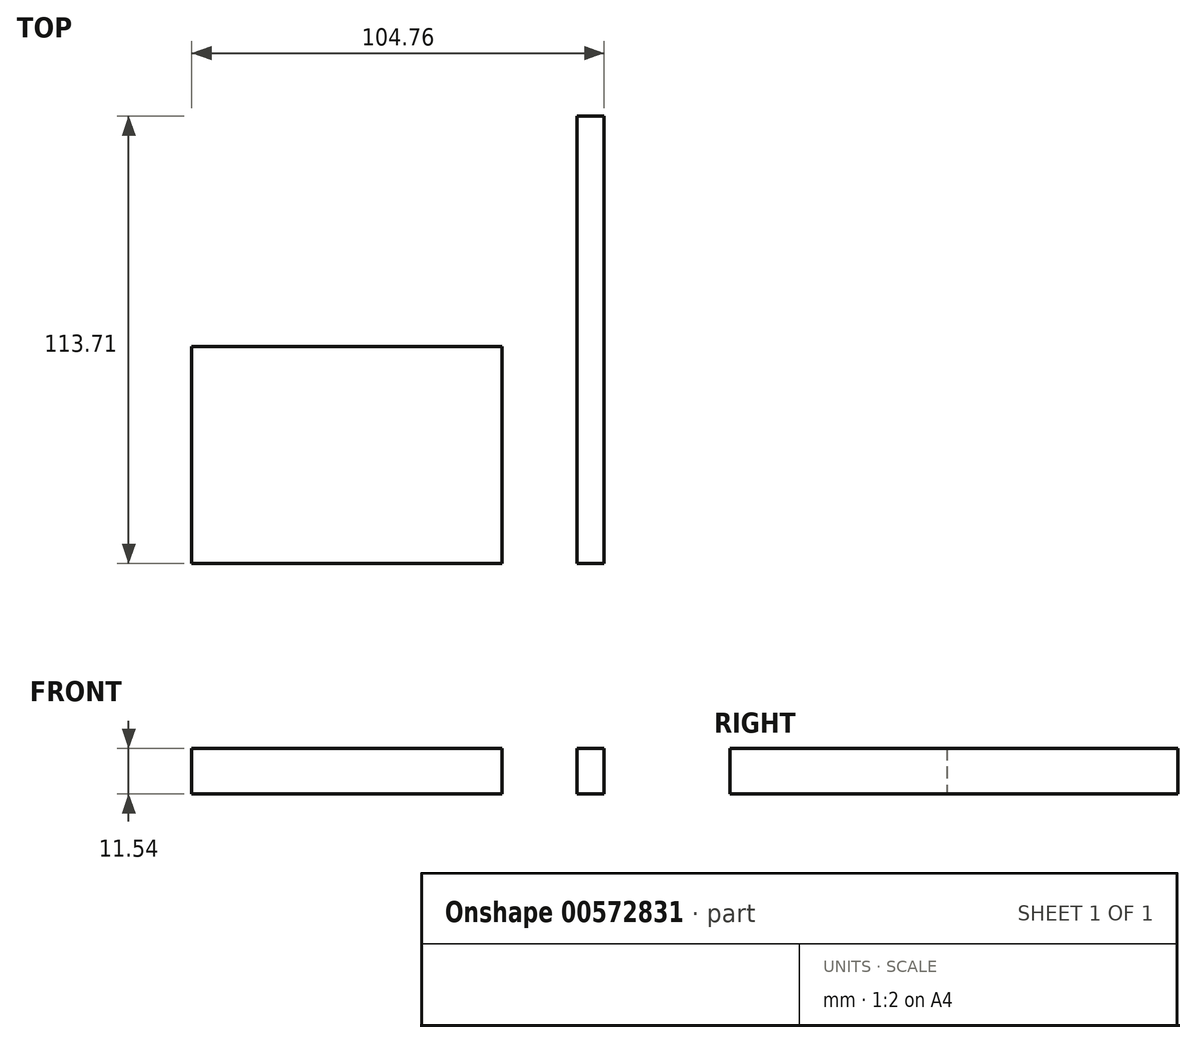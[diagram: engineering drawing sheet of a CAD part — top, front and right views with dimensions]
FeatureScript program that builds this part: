
annotation { "Feature Type Name" : "Feature", "Feature Type Description" : "" }
export const myFeature = defineFeature(function(context is Context, id is Id, definition is map)
    precondition{}
    {
        {
            var Q0;
            Q0=qCreatedBy(makeId("Top.planeOp"),FACE);
            var sketch = newSketch(context, id + "F0", { "sketchPlane" : qUnion([Q0])});
            skLineSegment(sketch, "E0.bottom", {"start": v(49.78, -55.1) * mm, "end": v(56.7, -55.1) * mm});
            skLineSegment(sketch, "E0.top", {"start": v(49.78, 58.61) * mm, "end": v(56.7, 58.61) * mm});
            skLineSegment(sketch, "E0.left", {"start": v(49.78, -55.1) * mm, "end": v(49.78, 58.61) * mm});
            skLineSegment(sketch, "E0.right", {"start": v(56.7, -55.1) * mm, "end": v(56.7, 58.61) * mm});
            skLineSegment(sketch, "E1.bottom", {"start": v(-48.05, 0) * mm, "end": v(30.72, 0) * mm});
            skLineSegment(sketch, "E1.top", {"start": v(-48.05, -55.1) * mm, "end": v(30.72, -55.1) * mm});
            skLineSegment(sketch, "E1.left", {"start": v(-48.05, 0) * mm, "end": v(-48.05, -55.1) * mm});
            skLineSegment(sketch, "E1.right", {"start": v(30.72, 0) * mm, "end": v(30.72, -55.1) * mm});
            skSolve(sketch);
        }
        {
            var Q0;
            Q0 = qSketchRegion(id + "F0", true);
            extrude(context, id + "F1", {"entities" : qUnion([Q0]), "depth" : 11.54 * mm, "offsetDistance" : 25.4 * mm});
        }
    });
